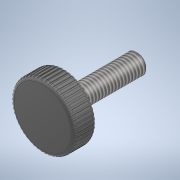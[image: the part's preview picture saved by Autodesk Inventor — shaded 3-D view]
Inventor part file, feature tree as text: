
AUTODESK INVENTOR PART (.ipt)
format: ipt  version: 2020 (Build 240168000, 168)  size: 466,432 bytes
history: native  units: mm
features: projected_geometry x5, extrude x4, sketch x4, fillet x2, chamfer x1, thread x1, pattern_circular x1
ambient origin geometry x8: Origin, YZ Plane, XZ Plane, XY Plane, X Axis, Y Axis, Z Axis, Center Point
bodies: Solid1 (feature_tree)
feature tree (18):
  extrude  "Extrusion1"  Depth=4.4mm TaperAngle=0.0deg
  extrude  "Extrusion2"  Depth=10.0mm TaperAngle=0.0deg
  extrude  "Extrusion3"  Depth=0.25mm TaperAngle=0.0deg
  chamfer  "Chamfer1"  Distance=0.25mm Angle=45.0deg
  fillet  "Fillet1"  Radius=0.5mm
  fillet  "Fillet2"  Radius=0.25mm
  thread  "Thread1"  [1 undecoded]
  extrude  "Extrusion4"  Depth=0.25mm
  pattern_circular  "Circular Pattern1"  [2 undecoded]
  sketch  "Sketch1"  dims[d0=9.6mm d1=4.4mm d2=0.0mm]
  sketch  "Sketch2"  dims[d3=3.0mm d4=10.0mm d5=0.0mm]
  sketch  "Sketch3"  dims[d7=6.0mm d8=1.0mm d9=0.0mm d10=0.25mm d11=2.0mm d12=45.0deg d13=0.5mm d14=0.25mm d15=19.75mm d16=0.0mm]
  sketch  "Sketch4"  dims[d17=0.25mm d18=0.125mm d19=0.0mm d20=0.0mm d21=500.0mm d22=360.0deg]
  projected_geometry  "Project Cut Edges1"
  projected_geometry  "Project Cut Edges2"
  projected_geometry  "Project Cut Edges3"
  projected_geometry  "Project Cut Edges4"
  projected_geometry  "Project Cut Edges5"
note: 3 required parameter values undecoded (feature->parameter linkage not recoverable at this tier; creation-order binding heuristic only, values carry confidence <= 0.55)
